# Revit family: 63_UN_Floodlighting_Coreline Tempo Small Gen2_Signify
name_source: partatom
category: Lighting Fixtures
units: mm (PartAtom-declared; Revit-internal decimal feet)

## family parameters
Always vertical = Yes
Cut with Voids When Loaded = Yes
Light Source = No
OmniClass Number = 23.80.70.11.14.11
OmniClass Title = Downlights
Part Type = Normal
Room Calculation Point = Yes
Round Connector Dimension = Use Diameter
Shared = No
Work Plane-Based = No

## types (2) — shared parameters
Apparent Load = 28 VA
Assembly Code = 63.0
Description = IP66
Housing_Material = Aluminum 7175 T73 0 Hot Formed
IfcExportAs = IfcLightFixtureType
IfcExportType = USERDEFINED
Lamp = LED
Luminous Flux (lm) = 4900 lm
Manufacturer = Signify
Model = Coreline
Type Comments = Small Gen2
URL = https://www.signify.com
Voltage = 230 V
Wattage Comments = 28.4

## per-type parameters (varying)
| type | Light Source |
| Coreline tempo_BVP111_ID2163 | Geometry : Coreline tempo_BVP111_ID2163 |
| Coreline tempo_BVP111_ID2164 | Geometry : Coreline tempo_BVP111_ID2164 |

## geometry (parser evidence)
native form markers: Sweep x19
no freeform markers — native parametric forms only
